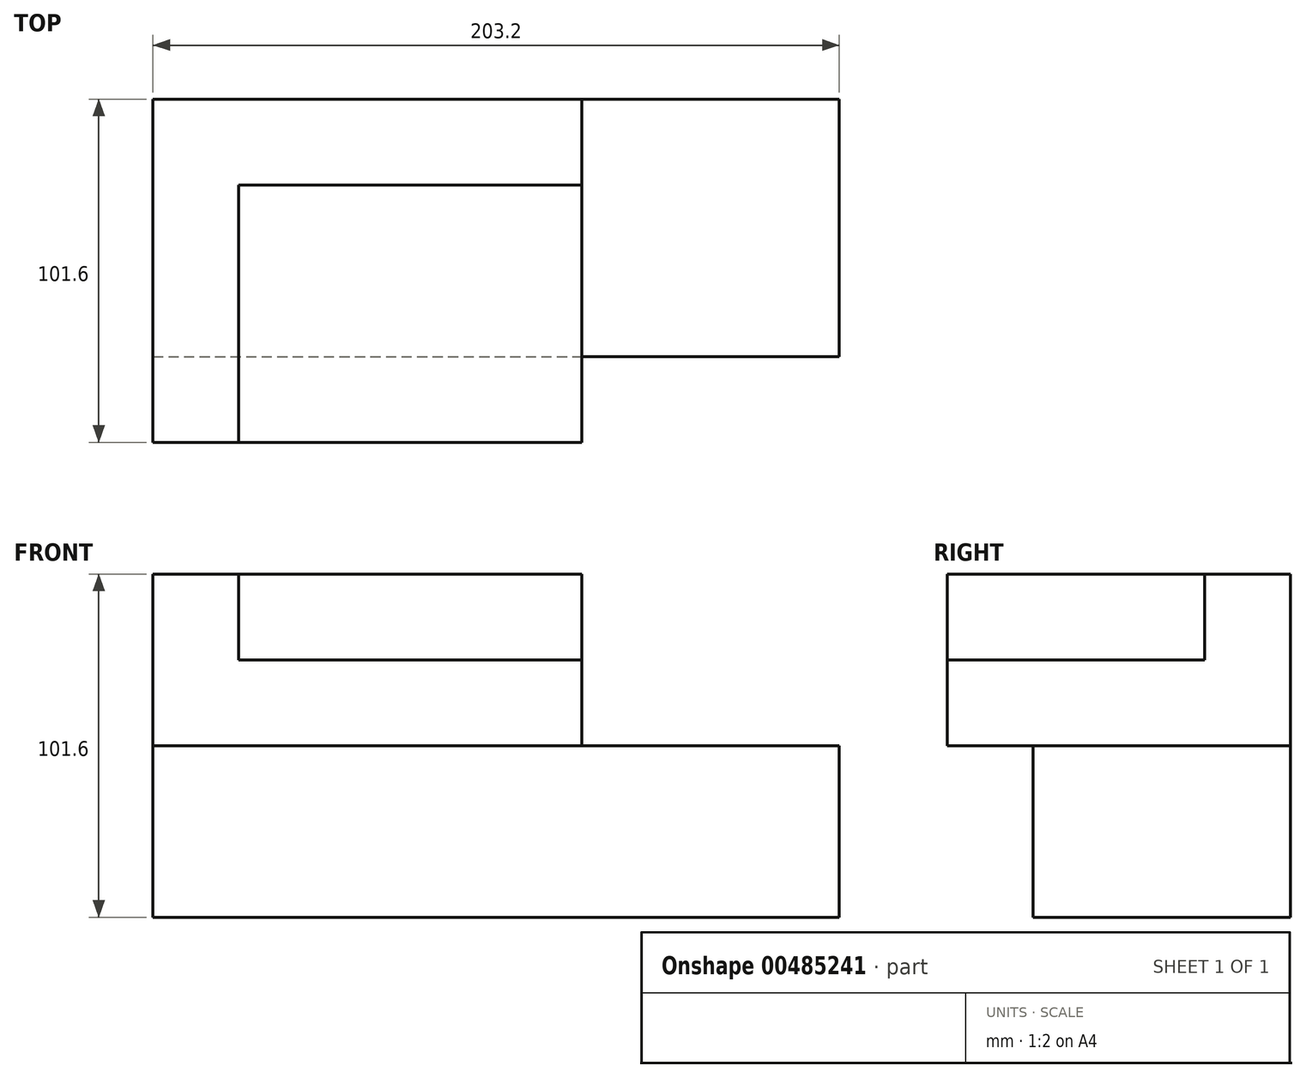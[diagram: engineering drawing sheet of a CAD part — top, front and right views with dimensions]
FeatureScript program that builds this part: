
annotation { "Feature Type Name" : "Feature", "Feature Type Description" : "" }
export const myFeature = defineFeature(function(context is Context, id is Id, definition is map)
    precondition{}
    {
        {
            var Q0;
            Q0=qCreatedBy(makeId("Front.planeOp"),FACE);
            var sketch = newSketch(context, id + "F0", { "sketchPlane" : qUnion([Q0])});
            skLineSegment(sketch, "E0.bottom", {"start": v(-84.95, 50.8) * mm, "end": v(42.05, 50.8) * mm});
            skLineSegment(sketch, "E0.top", {"start": v(-84.95, -50.8) * mm, "end": v(118.25, -50.8) * mm});
            skLineSegment(sketch, "E0.left", {"start": v(-84.95, 50.8) * mm, "end": v(-84.95, -50.8) * mm});
            skLineSegment(sketch, "E0.right", {"start": v(118.25, 0) * mm, "end": v(118.25, -50.8) * mm});
            skLineSegment(sketch, "E1", {"start": v(42.05, 50.8) * mm, "end": v(42.05, 0) * mm});
            skLineSegment(sketch, "E2", {"start": v(42.05, 0) * mm, "end": v(118.25, 0) * mm});
            skPoint(sketch, "E3.orphan", {"position": v(118.25, 50.8) * mm});
            skSolve(sketch);
        }
        {
            var Q0;
            Q0 = qSketchRegion(id + "F0", true);
            extrude(context, id + "F1", {"entities" : qUnion([Q0]), "depth" : 101.6 * mm});
        }
        {
            var Q0;
            Q0=makeQuery(id+"F1.opExtrude","SWEPT_FACE",FACE,{"disambiguationData":[OSD([sQuery(id+"F0.wireOp",EDGE,"E0.right")])]});
            var sketch = newSketch(context, id + "F2", { "sketchPlane" : qUnion([Q0])});
            skLineSegment(sketch, "E4.bottom", {"start": v(-101.6, 0) * mm, "end": v(-76.2, 0) * mm});
            skLineSegment(sketch, "E4.top", {"start": v(-101.6, -50.8) * mm, "end": v(-76.2, -50.8) * mm});
            skLineSegment(sketch, "E4.left", {"start": v(-101.6, 0) * mm, "end": v(-101.6, -50.8) * mm});
            skLineSegment(sketch, "E4.right", {"start": v(-76.2, 0) * mm, "end": v(-76.2, -50.8) * mm});
            skSolve(sketch);
        }
        {
            var Q0;
            Q0 = qSketchRegion(id + "F2", true);
            extrude(context, id + "F3", {"entities" : qUnion([Q0]), "operationType" : NewBodyOperationType.REMOVE, "oppositeDirection" : true, "depth" : 203.2 * mm});
        }
        {
            var Q0;
            Q0=makeQuery(id+"F1.opExtrude","SWEPT_FACE",FACE,{"disambiguationData":[OSD([sQuery(id+"F0.wireOp",EDGE,"E0.bottom")])]});
            var sketch = newSketch(context, id + "F4", { "sketchPlane" : qUnion([Q0])});
            skLineSegment(sketch, "E5.bottom", {"start": v(-59.55, -101.6) * mm, "end": v(42.05, -101.6) * mm});
            skLineSegment(sketch, "E5.top", {"start": v(-59.55, -25.4) * mm, "end": v(42.05, -25.4) * mm});
            skLineSegment(sketch, "E5.left", {"start": v(-59.55, -101.6) * mm, "end": v(-59.55, -25.4) * mm});
            skLineSegment(sketch, "E5.right", {"start": v(42.05, -101.6) * mm, "end": v(42.05, -25.4) * mm});
            skSolve(sketch);
        }
        {
            var Q0;
            Q0=makeQuery(id+"F4.imprint","IMPRINT",FACE,{"disambiguationData":[TD([[makeQuery(id+"F4.imprint","IMPRINT",EDGE,{"derivedFrom":sQuery(id+"F4.wireOp",EDGE,"E5.bottom")}),1.0]])]});
            extrude(context, id + "F5", {"entities" : qUnion([Q0]), "operationType" : NewBodyOperationType.REMOVE, "oppositeDirection" : true, "depth" : 25.4 * mm});
        }
    });
